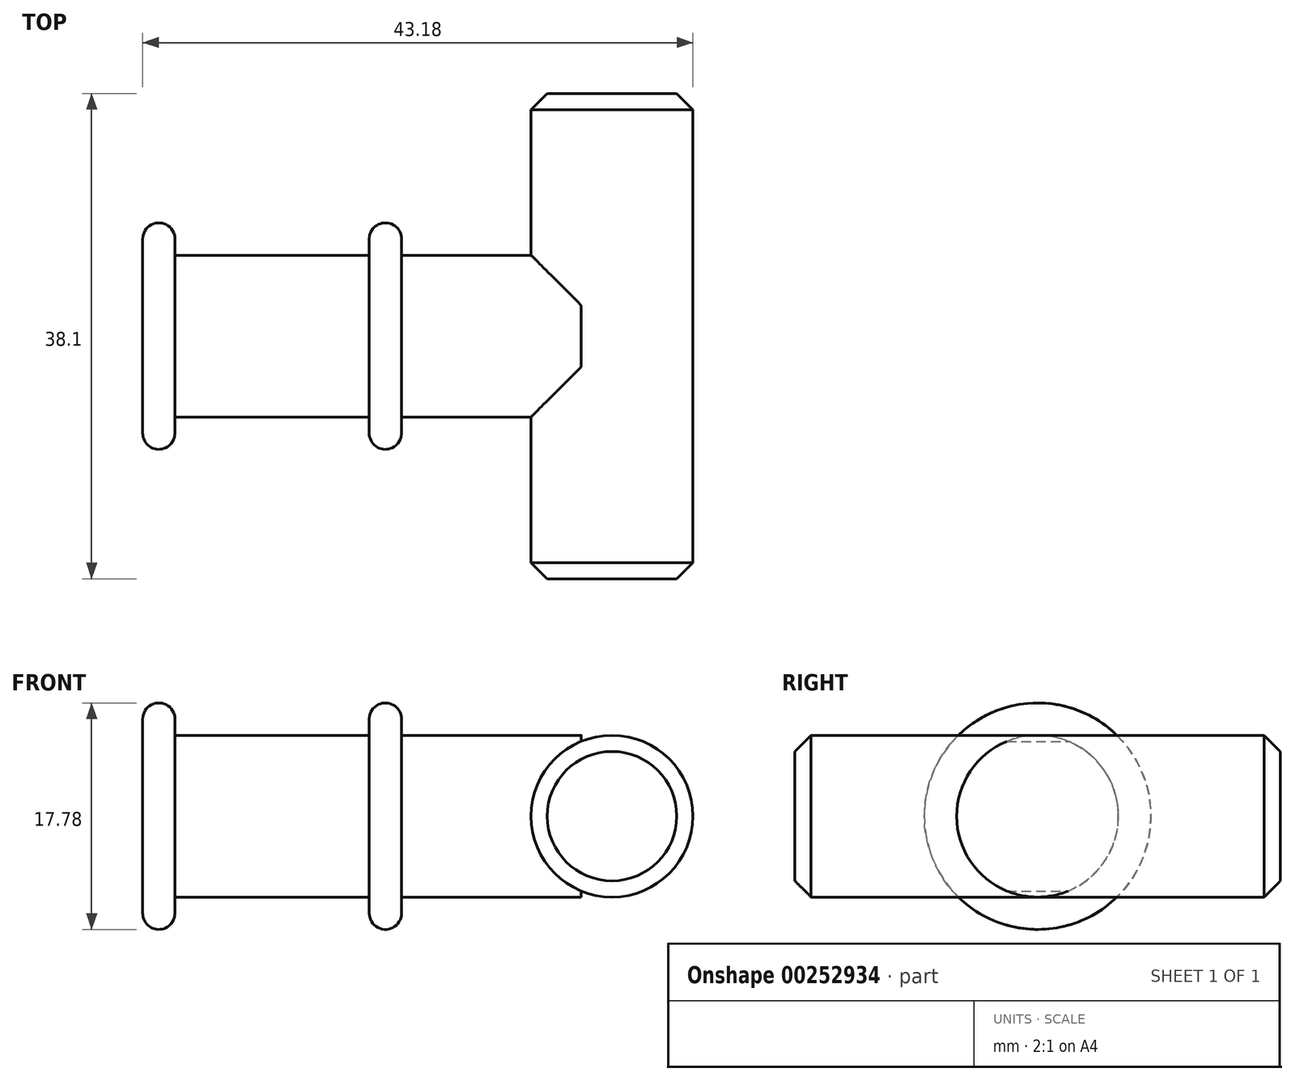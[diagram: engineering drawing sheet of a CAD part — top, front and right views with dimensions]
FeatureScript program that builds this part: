
annotation { "Feature Type Name" : "Feature", "Feature Type Description" : "" }
export const myFeature = defineFeature(function(context is Context, id is Id, definition is map)
    precondition{}
    {
        {
            var Q0;
            Q0=qCreatedBy(makeId("Right.planeOp"),FACE);
            var sketch = newSketch(context, id + "F0", { "sketchPlane" : qUnion([Q0])});
            skCircle(sketch, "E0", {"center": v(0, 182.4) * mm, "radius": 6.35 * mm});
            skSolve(sketch);
        }
        {
            var Q0;
            Q0 = qSketchRegion(id + "F0", true);
            extrude(context, id + "F1", {"entities" : qUnion([Q0]), "depth" : 15.24 * mm});
        }
        {
            var Q0;
            Q0=makeQuery(id+"F1.opExtrude","CAP_FACE",FACE,{"disambiguationData":[OSD([sQuery(id+"F0.wireOp",EDGE,"E0")])],"isStart":true});
            var sketch = newSketch(context, id + "F2", { "sketchPlane" : qUnion([Q0])});
            skCircle(sketch, "E1", {"center": v(0, 182.4) * mm, "radius": 8.9 * mm});
            skSolve(sketch);
        }
        {
            var Q0;
            Q0 = qSketchRegion(id + "F2", true);
            extrude(context, id + "F3", {"entities" : qUnion([Q0]), "operationType" : NewBodyOperationType.ADD, "depth" : 2.54 * mm});
        }
        {
            var Q0;
            Q0=makeQuery(id+"F3.opExtrude","SWEPT_FACE",FACE,{"disambiguationData":[OSD([sQuery(id+"F2.wireOp",EDGE,"E1")])]});
            fillet(context, id + "F4", {"entities" : qUnion([Q0]), "radius" : 1.27 * mm, "tangentPropagation" : true, "allowEdgeOverflow" : false});
        }
        {
            var Q0;
            Q0=makeQuery(id+"F1.opExtrude","CAP_FACE",FACE,{"disambiguationData":[OSD([sQuery(id+"F0.wireOp",EDGE,"E0")])],"isStart":false});
            var sketch = newSketch(context, id + "F5", { "sketchPlane" : qUnion([Q0])});
            skCircle(sketch, "E2", {"center": v(0, 182.4) * mm, "radius": 8.9 * mm});
            skSolve(sketch);
        }
        {
            var Q0;
            Q0 = qSketchRegion(id + "F5", true);
            extrude(context, id + "F6", {"entities" : qUnion([Q0]), "operationType" : NewBodyOperationType.ADD, "depth" : 2.54 * mm});
        }
        {
            var Q0;
            Q0=makeQuery(id+"F6.opExtrude","SWEPT_FACE",FACE,{"disambiguationData":[OSD([sQuery(id+"F5.wireOp",EDGE,"E2")])]});
            fillet(context, id + "F7", {"entities" : qUnion([Q0]), "radius" : 1.27 * mm, "tangentPropagation" : true, "allowEdgeOverflow" : false});
        }
        {
            var Q0;
            Q0=qCreatedBy(makeId("Front.planeOp"),FACE);
            var sketch = newSketch(context, id + "F8", { "sketchPlane" : qUnion([Q0])});
            skCircle(sketch, "E3", {"center": v(34.3, 182.4) * mm, "radius": 6.35 * mm});
            skSolve(sketch);
        }
        {
            var Q0;
            Q0 = qSketchRegion(id + "F8", true);
            extrude(context, id + "F9", {"entities" : qUnion([Q0]), "endBound" : BoundingType.SYMMETRIC, "depth" : 38.1 * mm});
        }
        {
            var Q0;
            Q0=makeQuery(id+"F6.opExtrude","CAP_FACE",FACE,{"disambiguationData":[OSD([sQuery(id+"F5.wireOp",EDGE,"E2")])],"isStart":false});
            var sketch = newSketch(context, id + "F10", { "sketchPlane" : qUnion([Q0])});
            skCircle(sketch, "E4", {"center": v(0, 182.4) * mm, "radius": 6.35 * mm});
            skSolve(sketch);
        }
        {
            var Q0;
            Q0 = qSketchRegion(id + "F10", true);
            var Q1;
            Q1=sQuery(id+"F10.wireOp",EDGE,"E4");
            extrude(context, id + "F11", {"entities" : qUnion([Q0]), "operationType" : NewBodyOperationType.ADD, "surfaceEntities" : qUnion([Q1]), "depth" : 14.1 * mm});
        }
        {
            var Q0;
            Q0=makeQuery(id+"F9.opExtrude","CAP_EDGE",EDGE,{"disambiguationData":[OSD([sQuery(id+"F8.wireOp",EDGE,"E3")])],"isStart":false});
            var Q1;
            Q1=makeQuery(id+"F9.opExtrude","CAP_EDGE",EDGE,{"disambiguationData":[OSD([sQuery(id+"F8.wireOp",EDGE,"E3")])],"isStart":true});
            chamfer(context, id + "F12", {"entities" : qUnion([Q0, Q1]), "width" : 1.27 * mm, "tangentPropagation" : true});
        }
        {
            var Q0;
            Q0=qCreatedBy(makeId("Front.planeOp"),FACE);
            var sketch = newSketch(context, id + "F13", { "sketchPlane" : qUnion([Q0])});
            skPoint(sketch, "E5", {"position": v(15.24, 182.4) * mm});
            skLineSegment(sketch, "E6", {"start": v(15.24, 182.4) * mm, "end": v(0, 0) * mm, "construction": true});
            skSolve(sketch);
        }
        {
            var Q0;
            Q0=makeQuery(id+"F1.opExtrude","SWEPT_BODY",BODY,{"disambiguationData":[OSD([sQuery(id+"F0.wireOp",EDGE,"E0")])]});
            var Q1;
            Q1=sQuery(id+"F13.wireOp",EDGE,"E6");
            transform(context, id + "F14", {"entities" : qUnion([Q0]), "transformType" : TransformType.TRANSLATION_ENTITY, "oppositeDirectionEntity" : false, "transformLine" : qUnion([Q1]), "makeCopy" : false});
        }
    });
